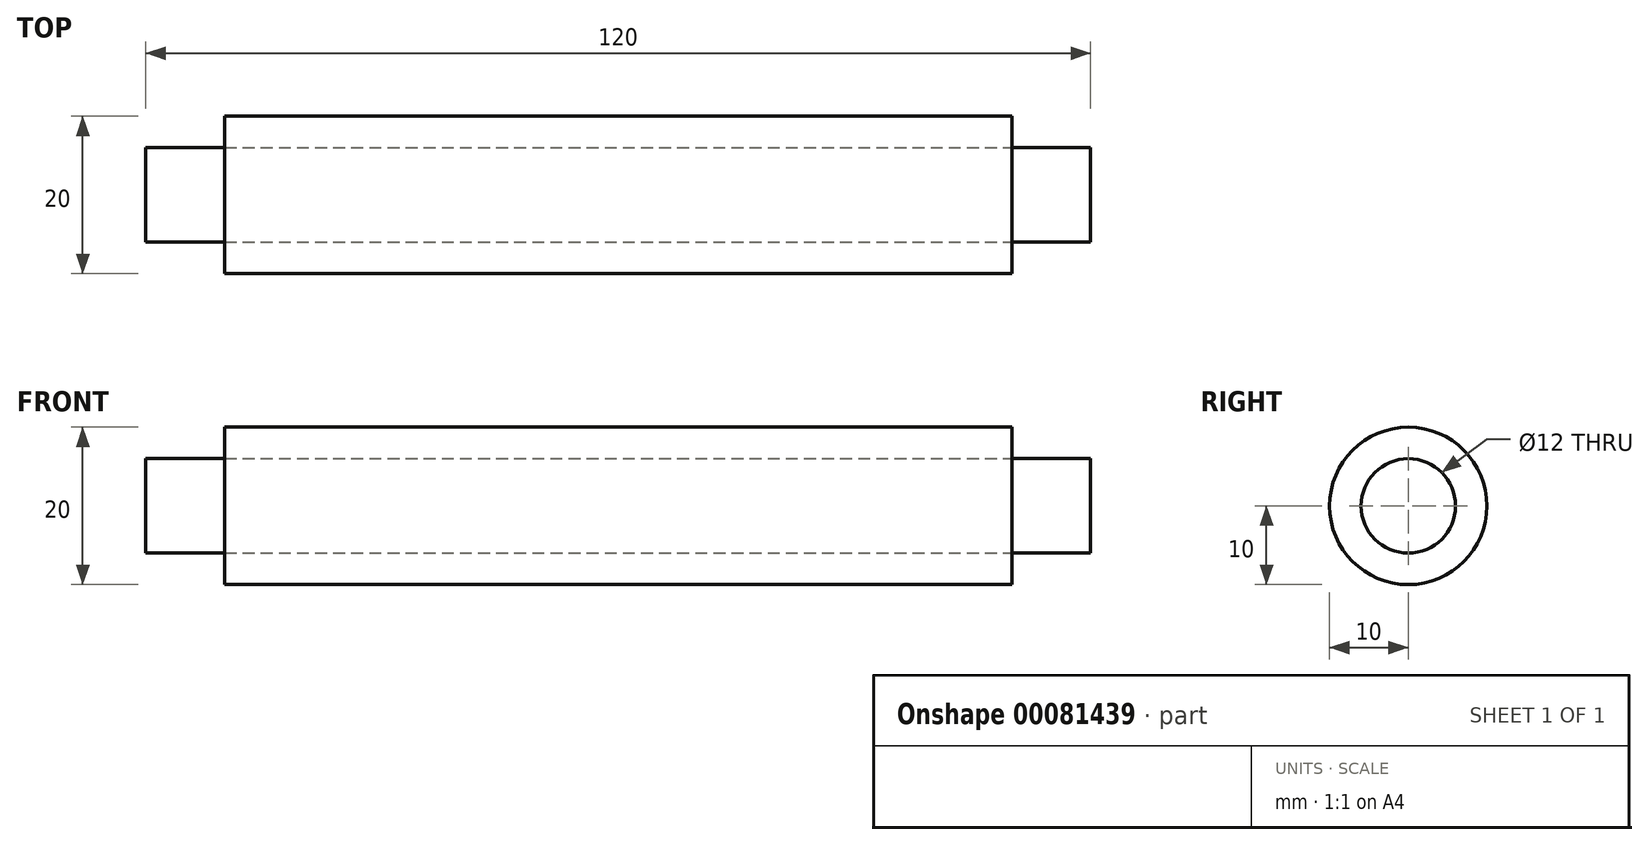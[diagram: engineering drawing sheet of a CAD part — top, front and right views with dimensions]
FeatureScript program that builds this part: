
annotation { "Feature Type Name" : "Feature", "Feature Type Description" : "" }
export const myFeature = defineFeature(function(context is Context, id is Id, definition is map)
    precondition{}
    {
        {
            var Q0;
            Q0=qCreatedBy(makeId("Front.planeOp"),FACE);
            var sketch = newSketch(context, id + "F0", { "sketchPlane" : qUnion([Q0])});
            skLineSegment(sketch, "E0", {"start": v(62.94, 0) * mm, "end": v(-103.67, 0) * mm, "construction": true});
            skLineSegment(sketch, "E1.bottom", {"start": v(-83.85, 0) * mm, "end": v(36.15, 0) * mm});
            skLineSegment(sketch, "E1.top", {"start": v(-83.85, 6) * mm, "end": v(36.15, 6) * mm});
            skLineSegment(sketch, "E1.left", {"start": v(-83.85, 0) * mm, "end": v(-83.85, 6) * mm});
            skLineSegment(sketch, "E1.right", {"start": v(36.15, 0) * mm, "end": v(36.15, 6) * mm});
            skLineSegment(sketch, "E2.bottom", {"start": v(26.15, 0) * mm, "end": v(-73.85, 0) * mm});
            skLineSegment(sketch, "E2.top", {"start": v(26.15, 10) * mm, "end": v(-73.85, 10) * mm});
            skLineSegment(sketch, "E2.left", {"start": v(26.15, 0) * mm, "end": v(26.15, 10) * mm});
            skLineSegment(sketch, "E2.right", {"start": v(-73.85, 0) * mm, "end": v(-73.85, 10) * mm});
            skSolve(sketch);
        }
        {
            var Q0;
            {var subQ0=sQuery(id+"F0.wireOp",EDGE,"E1.left");Q0=makeQuery(id+"F0.imprint","IMPRINT",FACE,{"disambiguationData":[TD([[makeQuery(id+"F0.imprint","IMPRINT",EDGE,{"derivedFrom":subQ0}),-1.0]])]});}
            var Q1;
            {var subQ5=sQuery(id+"F0.wireOp",EDGE,"E2.bottom");Q1=makeQuery(id+"F0.imprint","IMPRINT",FACE,{"disambiguationData":[TD([[makeQuery(id+"F0.imprint","IMPRINT",EDGE,{"derivedFrom":subQ5}),-1.0]])]});}
            var Q2;
            {var subQ5=sQuery(id+"F0.wireOp",EDGE,"E2.top");Q2=makeQuery(id+"F0.imprint","IMPRINT",FACE,{"disambiguationData":[TD([[makeQuery(id+"F0.imprint","IMPRINT",EDGE,{"derivedFrom":subQ5}),1.0]])]});}
            var Q3;
            {var subQ0=sQuery(id+"F0.wireOp",EDGE,"E1.right");Q3=makeQuery(id+"F0.imprint","IMPRINT",FACE,{"disambiguationData":[TD([[makeQuery(id+"F0.imprint","IMPRINT",EDGE,{"derivedFrom":subQ0}),1.0]])]});}
            var Q4;
            Q4=sQuery(id+"F0.wireOp",EDGE,"E0");
            revolve(context, id + "F1", {"entities" : qUnion([Q0, Q1, Q2, Q3]), "axis" : qUnion([Q4]), "revolveType" : RevolveType.FULL});
        }
    });
